# Revit family: GEA
name_source: partatom
category: Air Terminals
revit_build: Autodesk Revit MEP 2012 (Build: 20110309_2315(x64)
units: mm (PartAtom-declared; Revit-internal decimal feet)

## types (4) — shared parameters
Alto rejilla = 3/4"
Ancho barra = 1/16"
Ancho rejillla = 5/32"
Largo barra = 15/64"
Manufacturer = INNES
Máxima presión estática = 0.00 in-wg
Máxima velocidad de cuello = 0 FPM
Mínima presión estática = 0.00 in-wg
Mínima velocidad de cuello = 0 FPM
Separacion = 5/16"
Separacion barras = 61/64"
URL = http://www.innes.com.mx

## per-type parameters (varying)
| type | Ancho A | Ancho B | Ancho barras | Largo A | Largo B | No. de elementos | No. de elementos barras |
| GEA-07-11 | 12 11/64" | 10 7/8" | 10 3/32" | 8 7/8" | 6 7/8" | 15 | 11 |
| GEA-08-12 | 13 11/64" | 11 7/8" | 11 3/32" | 9 7/8" | 7 7/8" | 17 | 12 |
| GEA-09-13 | 14 11/64" | 12 7/8" | 12 3/32" | 10 7/8" | 8 7/8" | 19 | 13 |
| GEA-10-14 | 15 11/64" | 13 7/8" | 13 3/32" | 11 7/8" | 9 7/8" | 21 | 14 |

## geometry (parser evidence)
native form markers: Sweep x8
no freeform markers — native parametric forms only
